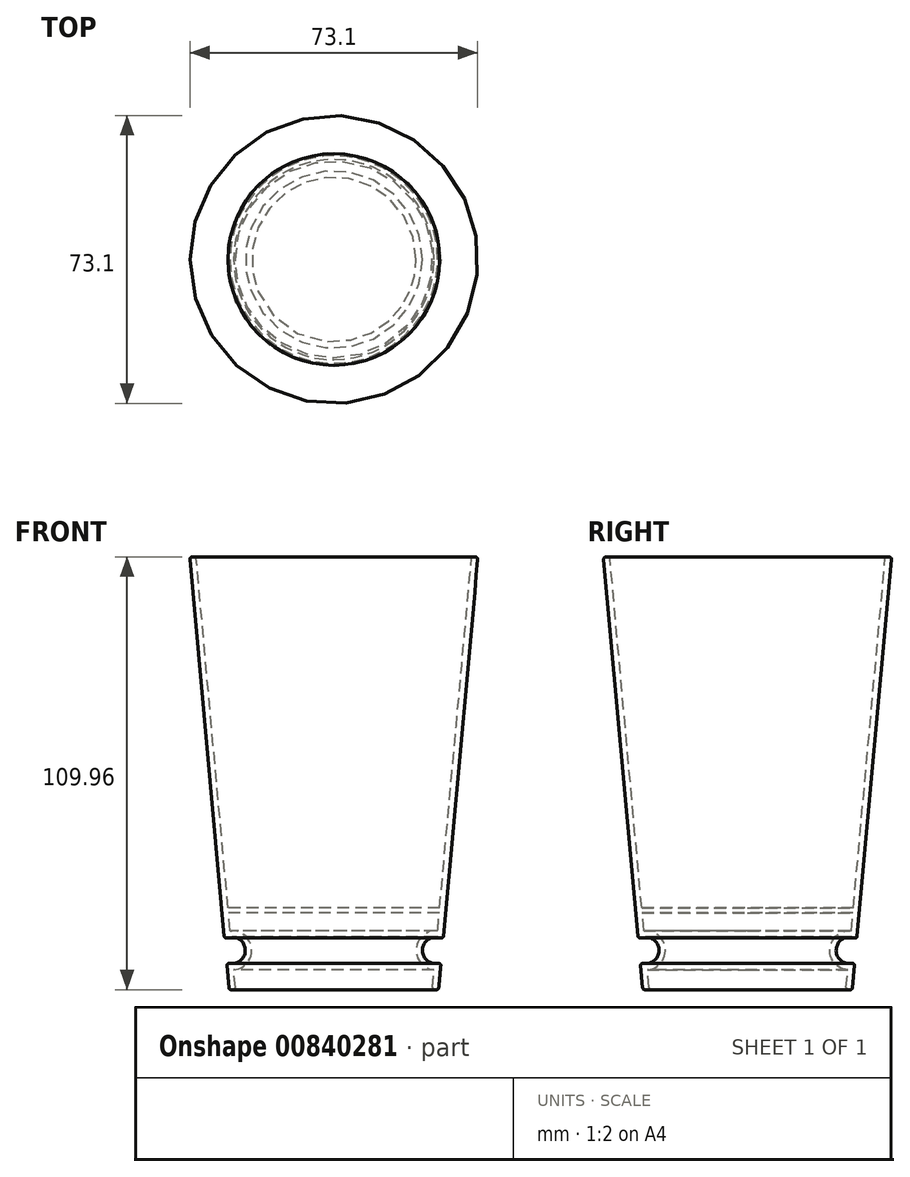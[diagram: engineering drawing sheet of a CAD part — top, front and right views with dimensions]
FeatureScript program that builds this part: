
annotation { "Feature Type Name" : "Feature", "Feature Type Description" : "" }
export const myFeature = defineFeature(function(context is Context, id is Id, definition is map)
    precondition{}
    {
        {
            var Q0;
            Q0=qCreatedBy(makeId("Front.planeOp"),FACE);
            var sketch = newSketch(context, id + "F0", { "sketchPlane" : qUnion([Q0])});
            skLineSegment(sketch, "E0", {"start": v(25, 0) * mm, "end": v(25.45, 5.02) * mm});
            skArc(sketch, "E1", {"start": v(26.36, 14.98) * mm, "mid": v(20.92, 10.45) * mm, "end": v(25.45, 5.02) * mm});
            skLineSegment(sketch, "E2.trimOffspring", {"start": v(26.36, 14.98) * mm, "end": v(26.77, 19.54) * mm});
            skLineSegment(sketch, "E3.0", {"start": v(27.77, 12.84) * mm, "end": v(36.6, 109.86) * mm});
            skArc(sketch, "E3.1", {"start": v(27.77, 12.84) * mm, "mid": v(22.52, 10.3) * mm, "end": v(27.23, 6.87) * mm});
            skLineSegment(sketch, "E3.2", {"start": v(26.6, 0) * mm, "end": v(27.23, 6.87) * mm});
            skLineSegment(sketch, "E4", {"start": v(26.77, 19.54) * mm, "end": v(0, 19.54) * mm});
            skLineSegment(sketch, "E5.0", {"start": v(26.88, 20.74) * mm, "end": v(0, 20.74) * mm});
            skLineSegment(sketch, "E6.trimOffspring", {"start": v(26.88, 20.74) * mm, "end": v(35, 110) * mm});
            skLineSegment(sketch, "E7", {"start": v(36.6, 109.86) * mm, "end": v(35, 110) * mm});
            skLineSegment(sketch, "E8", {"start": v(26.6, 0) * mm, "end": v(25, 0) * mm});
            skLineSegment(sketch, "E9", {"start": v(0, 19.54) * mm, "end": v(0, 20.74) * mm});
            skSolve(sketch);
        }
        {
            var Q0;
            Q0=qCreatedBy(makeId("Front.planeOp"),FACE);
            var sketch = newSketch(context, id + "F1", { "sketchPlane" : qUnion([Q0])});
            skLineSegment(sketch, "E10", {"start": v(0, 60.96) * mm, "end": v(0, 49.66) * mm});
            skSolve(sketch);
        }
        {
            var Q0;
            Q0 = qSketchRegion(id + "F0", true);
            var Q1;
            Q1=sQuery(id+"F1.wireOp",EDGE,"E10");
            revolve(context, id + "F2", {"surfaceOperationType" : NewSurfaceOperationType.NEW, "entities" : qUnion([Q0]), "axis" : qUnion([Q1]), "revolveType" : RevolveType.FULL});
        }
        {
            var Q0;
            Q0=makeQuery(id+"F2.opRevolve","SWEPT_EDGE",EDGE,{"disambiguationData":[OSD([sQuery(id+"F0.wireOp",EDGE,"E3.0"),sQuery(id+"F0.wireOp",EDGE,"E3.1")])]});
            var Q1;
            Q1=makeQuery(id+"F2.opRevolve","SWEPT_EDGE",EDGE,{"disambiguationData":[OSD([sQuery(id+"F0.wireOp",EDGE,"E3.1"),sQuery(id+"F0.wireOp",EDGE,"E3.2")])]});
            var Q2;
            Q2=makeQuery(id+"F2.opRevolve","SWEPT_EDGE",EDGE,{"disambiguationData":[OSD([sQuery(id+"F0.wireOp",EDGE,"E3.2"),sQuery(id+"F0.wireOp",EDGE,"E8")])]});
            var Q3;
            Q3=makeQuery(id+"F2.opRevolve","SWEPT_EDGE",EDGE,{"disambiguationData":[OSD([sQuery(id+"F0.wireOp",EDGE,"E0"),sQuery(id+"F0.wireOp",EDGE,"E8")])]});
            var Q4;
            Q4=makeQuery(id+"F2.opRevolve","SWEPT_EDGE",EDGE,{"disambiguationData":[OSD([sQuery(id+"F0.wireOp",EDGE,"E3.0"),sQuery(id+"F0.wireOp",EDGE,"E7")])]});
            var Q5;
            Q5=makeQuery(id+"F2.opRevolve","SWEPT_EDGE",EDGE,{"disambiguationData":[OSD([sQuery(id+"F0.wireOp",EDGE,"E6.trimOffspring"),sQuery(id+"F0.wireOp",EDGE,"E7")])]});
            fillet(context, id + "F3", {"entities" : qUnion([Q0, Q1, Q2, Q3, Q4, Q5]), "radius" : 0.5 * mm, "tangentPropagation" : true, "allowEdgeOverflow" : false});
        }
    });
